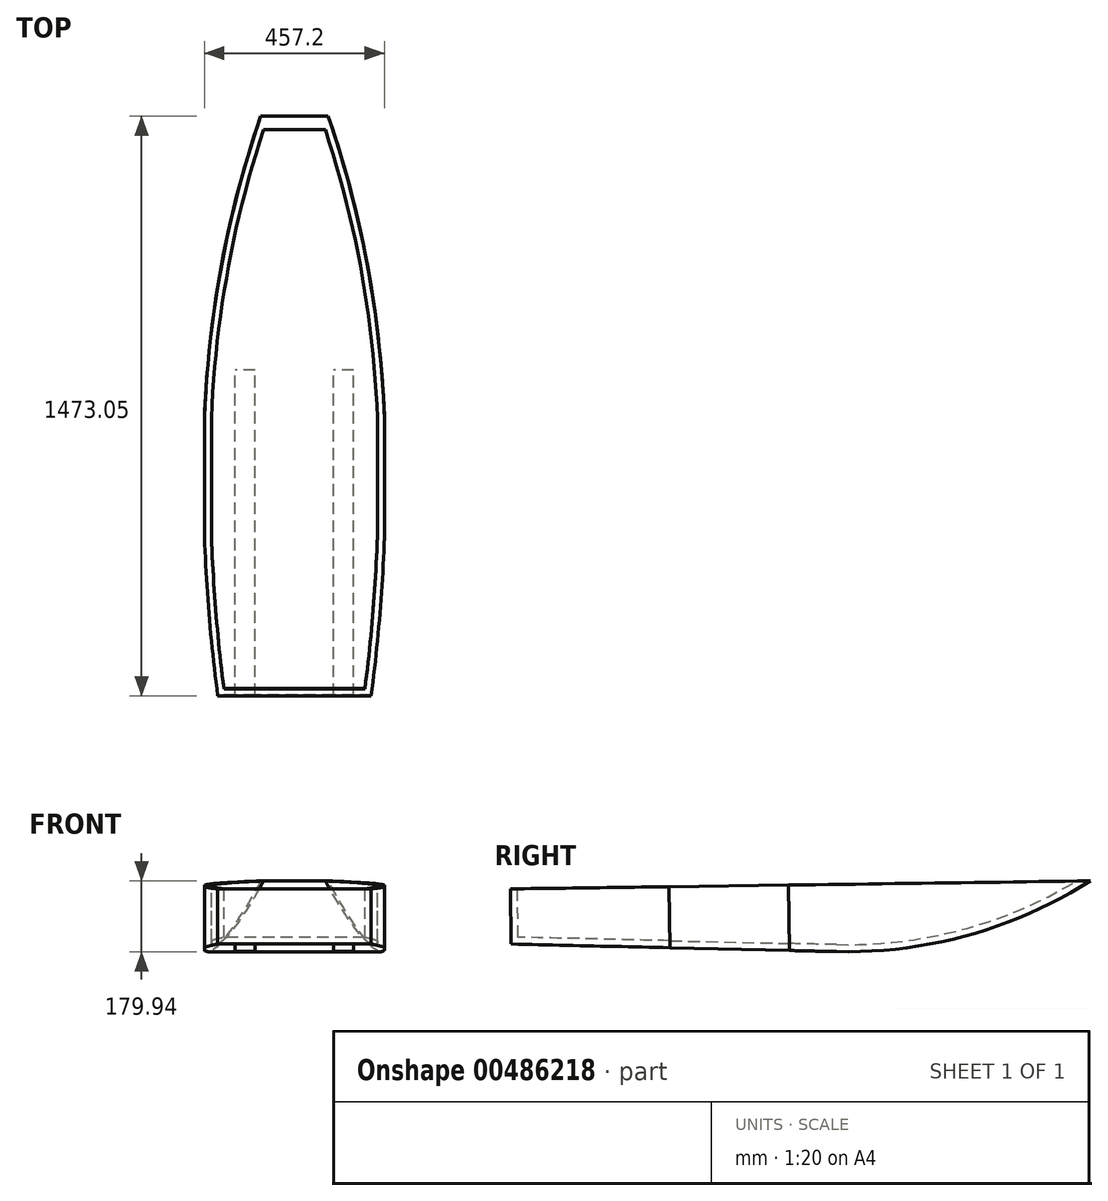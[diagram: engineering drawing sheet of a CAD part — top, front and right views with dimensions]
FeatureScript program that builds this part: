
annotation { "Feature Type Name" : "Feature", "Feature Type Description" : "" }
export const myFeature = defineFeature(function(context is Context, id is Id, definition is map)
    precondition{}
    {
        {
            var Q0;
            Q0=qCreatedBy(makeId("Right.planeOp"),FACE);
            var sketch = newSketch(context, id + "F0", { "sketchPlane" : qUnion([Q0])});
            skLineSegment(sketch, "E0", {"start": v(-641.11, -283.27) * mm, "end": v(-641.11, -423.3) * mm});
            skLineSegment(sketch, "E1", {"start": v(-641.11, -423.3) * mm, "end": v(187.44, -442.56) * mm});
            skLineSegment(sketch, "E2", {"start": v(-641.11, -283.27) * mm, "end": v(288.92, -270.43) * mm});
            skLineSegment(sketch, "E3", {"start": v(-641.11, -283.27) * mm, "end": v(831.94, -262.93) * mm, "construction": true});
            skArc(sketch, "E4", {"start": v(187.44, -442.56) * mm, "mid": v(523.04, -400.64) * mm, "end": v(831.94, -262.93) * mm});
            skLineSegment(sketch, "E5", {"start": v(288.92, -270.43) * mm, "end": v(831.94, -262.93) * mm});
            skSolve(sketch);
        }
        {
            var Q0;
            Q0 = qSketchRegion(id + "F0", true);
            extrude(context, id + "F1", {"entities" : qUnion([Q0]), "depth" : 457.2 * mm, "offsetDistance" : 25.4 * mm});
        }
        {
            var Q0;
            Q0=makeQuery(id+"F1.opExtrude","SWEPT_FACE",FACE,{"disambiguationData":[OSD([sQuery(id+"F0.wireOp",EDGE,"E2"),sQuery(id+"F0.wireOp",EDGE,"E5")])]});
            var sketch = newSketch(context, id + "F2", { "sketchPlane" : qUnion([Q0])});
            skLineSegment(sketch, "E6", {"start": v(228.6, 828.23) * mm, "end": v(457.2, 828.23) * mm, "construction": true});
            skLineSegment(sketch, "E7", {"start": v(457.2, 828.23) * mm, "end": v(0, 828.23) * mm, "construction": true});
            skLineSegment(sketch, "E8", {"start": v(0, 828.23) * mm, "end": v(228.6, 828.23) * mm, "construction": true});
            skLineSegment(sketch, "E9", {"start": v(114.3, 828.23) * mm, "end": v(228.6, 828.23) * mm, "construction": true});
            skLineSegment(sketch, "E10", {"start": v(342.9, 828.23) * mm, "end": v(228.6, 828.23) * mm, "construction": true});
            skLineSegment(sketch, "E11", {"start": v(285.75, 828.23) * mm, "end": v(342.9, 828.23) * mm, "construction": true});
            skLineSegment(sketch, "E12", {"start": v(228.6, 828.23) * mm, "end": v(171.45, 828.23) * mm, "construction": true});
            skLineSegment(sketch, "E13", {"start": v(114.3, 828.23) * mm, "end": v(171.45, 828.23) * mm, "construction": true});
            skArc(sketch, "E14", {"start": v(142.88, 828.23) * mm, "mid": v(43.6, 450.08) * mm, "end": v(0, 61.55) * mm});
            skLineSegment(sketch, "E15", {"start": v(228.6, 828.23) * mm, "end": v(228.6, 573.2) * mm, "construction": true});
            skArc(sketch, "E16.MirrorCS", {"start": v(314.33, 828.23) * mm, "mid": v(413.6, 450.08) * mm, "end": v(457.2, 61.55) * mm});
            skLineSegment(sketch, "E17", {"start": v(142.88, 828.23) * mm, "end": v(0, 828.23) * mm});
            skLineSegment(sketch, "E18", {"start": v(0, 61.55) * mm, "end": v(-26.32, 828.23) * mm});
            skLineSegment(sketch, "E19", {"start": v(-26.32, 828.23) * mm, "end": v(0, 828.23) * mm});
            skLineSegment(sketch, "E20.MirrorCS", {"start": v(457.2, 61.55) * mm, "end": v(483.52, 828.23) * mm});
            skLineSegment(sketch, "E21.MirrorCS", {"start": v(483.52, 828.23) * mm, "end": v(457.2, 828.23) * mm});
            skLineSegment(sketch, "E22.MirrorCS", {"start": v(314.33, 828.23) * mm, "end": v(457.2, 828.23) * mm});
            skLineSegment(sketch, "E23", {"start": v(423.38, -644.97) * mm, "end": v(615.9, -644.97) * mm});
            skLineSegment(sketch, "E24", {"start": v(615.9, -644.97) * mm, "end": v(483.52, 828.23) * mm});
            skLineSegment(sketch, "E25", {"start": v(33.82, -644.97) * mm, "end": v(-361.61, -644.97) * mm});
            skLineSegment(sketch, "E26", {"start": v(-361.61, -644.97) * mm, "end": v(-26.32, 828.23) * mm});
            skLineSegment(sketch, "E27", {"start": v(-361.61, -644.97) * mm, "end": v(237.29, -852.32) * mm});
            skLineSegment(sketch, "E28", {"start": v(237.29, -852.32) * mm, "end": v(615.9, -644.97) * mm});
            skArc(sketch, "E29", {"start": v(423.38, -644.97) * mm, "mid": v(455.08, -292.42) * mm, "end": v(457.2, 61.55) * mm});
            skArc(sketch, "E30.MirrorCS", {"start": v(33.82, -644.97) * mm, "mid": v(2.12, -292.42) * mm, "end": v(0, 61.55) * mm});
            skSolve(sketch);
        }
        {
            var Q0;
            Q0 = qSketchRegion(id + "F2", true);
            var Q1;
            {var subQ6=sQuery(id+"F2.wireOp",EDGE,"E27");Q1=makeQuery(id+"F2.imprint","IMPRINT",FACE,{"disambiguationData":[TD([[makeQuery(id+"F2.imprint","IMPRINT",EDGE,{"derivedFrom":subQ6}),1.0]])]});}
            extrude(context, id + "F3", {"entities" : qUnion([Q0, Q1]), "operationType" : NewBodyOperationType.REMOVE, "oppositeDirection" : true, "depth" : 254 * mm, "offsetDistance" : 25.4 * mm});
        }
        {
            var Q0;
            Q0=makeQuery(id+"F1.opExtrude","SWEPT_FACE",FACE,{"disambiguationData":[OSD([sQuery(id+"F0.wireOp",EDGE,"E2"),sQuery(id+"F0.wireOp",EDGE,"E5")])]});
            shell(context, id + "F4", {"entities" : qUnion([Q0]), "thickness" : 17.78 * mm});
        }
        {
            var Q0;
            Q0=makeQuery(id+"F1.opExtrude","SWEPT_FACE",FACE,{"disambiguationData":[OSD([sQuery(id+"F0.wireOp",EDGE,"E1")])]});
            var sketch = newSketch(context, id + "F5", { "sketchPlane" : qUnion([Q0])});
            skLineSegment(sketch, "E31.bottom", {"start": v(78.3, 629.17) * mm, "end": v(129.1, 629.17) * mm});
            skLineSegment(sketch, "E31.top", {"start": v(78.3, -197.68) * mm, "end": v(129.1, -197.68) * mm});
            skLineSegment(sketch, "E31.left", {"start": v(78.3, 629.17) * mm, "end": v(78.3, -197.68) * mm});
            skLineSegment(sketch, "E31.right", {"start": v(129.1, 629.17) * mm, "end": v(129.1, -197.68) * mm});
            skLineSegment(sketch, "E32", {"start": v(228.6, 629.17) * mm, "end": v(228.6, 389.45) * mm, "construction": true});
            skLineSegment(sketch, "E33.MirrorCS", {"start": v(328.1, 629.17) * mm, "end": v(328.1, -197.68) * mm});
            skLineSegment(sketch, "E34.MirrorCS", {"start": v(378.9, 629.17) * mm, "end": v(378.9, -197.68) * mm});
            skLineSegment(sketch, "E35.MirrorCS", {"start": v(378.9, -197.68) * mm, "end": v(328.1, -197.68) * mm});
            skLineSegment(sketch, "E36.MirrorCS", {"start": v(378.9, 629.17) * mm, "end": v(328.1, 629.17) * mm});
            skSolve(sketch);
        }
        {
            var Q0;
            Q0 = qSketchRegion(id + "F5", true);
            extrude(context, id + "F6", {"entities" : qUnion([Q0]), "operationType" : NewBodyOperationType.REMOVE, "oppositeDirection" : true, "depth" : 0.5 * mm, "offsetDistance" : 25.4 * mm});
        }
    });
